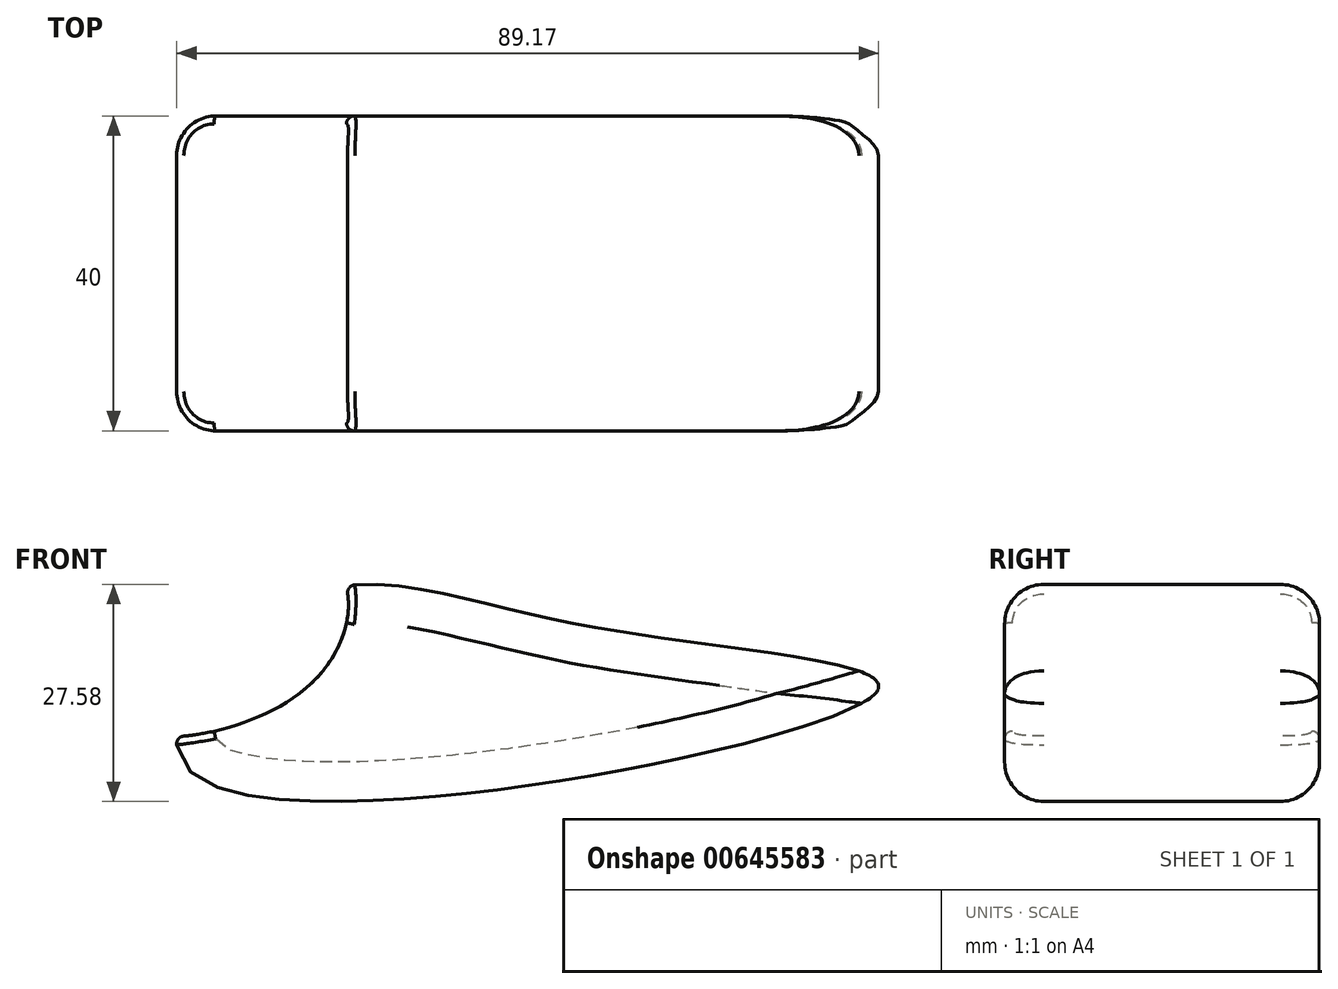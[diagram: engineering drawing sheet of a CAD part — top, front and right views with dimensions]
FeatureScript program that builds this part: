
annotation { "Feature Type Name" : "Feature", "Feature Type Description" : "" }
export const myFeature = defineFeature(function(context is Context, id is Id, definition is map)
    precondition{}
    {
        {
            var Q0;
            Q0=qCreatedBy(makeId("Front.planeOp"),FACE);
            var sketch = newSketch(context, id + "F0", { "sketchPlane" : qUnion([Q0])});
            skFitSpline(sketch, "E0", {"points": [v(-36.8, 0) * mm, v(-25.08, 21.58) * mm, v(12.64, 18.99) * mm, v(49.87, 10.36) * mm, v(-36.8, 0) * mm]});
            skSolve(sketch);
        }
        {
            var Q0;
            Q0=makeQuery(id+"F0.imprint","IMPRINT",FACE,{"disambiguationData":[TD([[makeQuery(id+"F0.imprint","IMPRINT",EDGE,{"derivedFrom":sQuery(id+"F0.wireOp",EDGE,"E0")}),-1.0]])]});
            extrude(context, id + "F1", {"entities" : qUnion([Q0]), "depth" : 40 * mm, "offsetDistance" : 25 * mm});
        }
        {
            var Q0;
            Q0=makeQuery(id+"F1.opExtrude","CAP_EDGE",EDGE,{"disambiguationData":[OSD([sQuery(id+"F0.wireOp",EDGE,"E0")])],"isStart":true});
            var Q1;
            Q1=makeQuery(id+"F1.opExtrude","CAP_EDGE",EDGE,{"disambiguationData":[OSD([sQuery(id+"F0.wireOp",EDGE,"E0")])],"isStart":false});
            fillet(context, id + "F2", {"entities" : qUnion([Q0, Q1]), "radius" : 5 * mm, "tangentPropagation" : true, "allowEdgeOverflow" : false});
        }
        {
            var Q0;
            Q0=qCreatedBy(makeId("Front.planeOp"),FACE);
            var sketch = newSketch(context, id + "F3", { "sketchPlane" : qUnion([Q0])});
            skFitSpline(sketch, "E1", {"points": [v(-18.4, 26.13) * mm, v(-22.69, 10.82) * mm, v(-46, 6.45) * mm, v(-42.93, 19.49) * mm, v(-31.03, 29.45) * mm, v(-18.4, 26.13) * mm]});
            skSolve(sketch);
        }
        {
            var Q0;
            Q0 = qSketchRegion(id + "F3", true);
            extrude(context, id + "F4", {"entities" : qUnion([Q0]), "operationType" : NewBodyOperationType.REMOVE, "depth" : 47.2 * mm, "offsetDistance" : 25 * mm});
        }
        {
            var Q0;
            Q0=makeQuery(id+"F4.boolean.opBoolean","COPY",FACE,{"derivedFrom":makeQuery(id+"F4.opExtrude","SWEPT_FACE",FACE,{"disambiguationData":[OSD([sQuery(id+"F3.wireOp",EDGE,"E1")])]})});
            fillet(context, id + "F5", {"entities" : qUnion([Q0]), "radius" : 1 * mm, "tangentPropagation" : true, "allowEdgeOverflow" : false});
        }
    });
